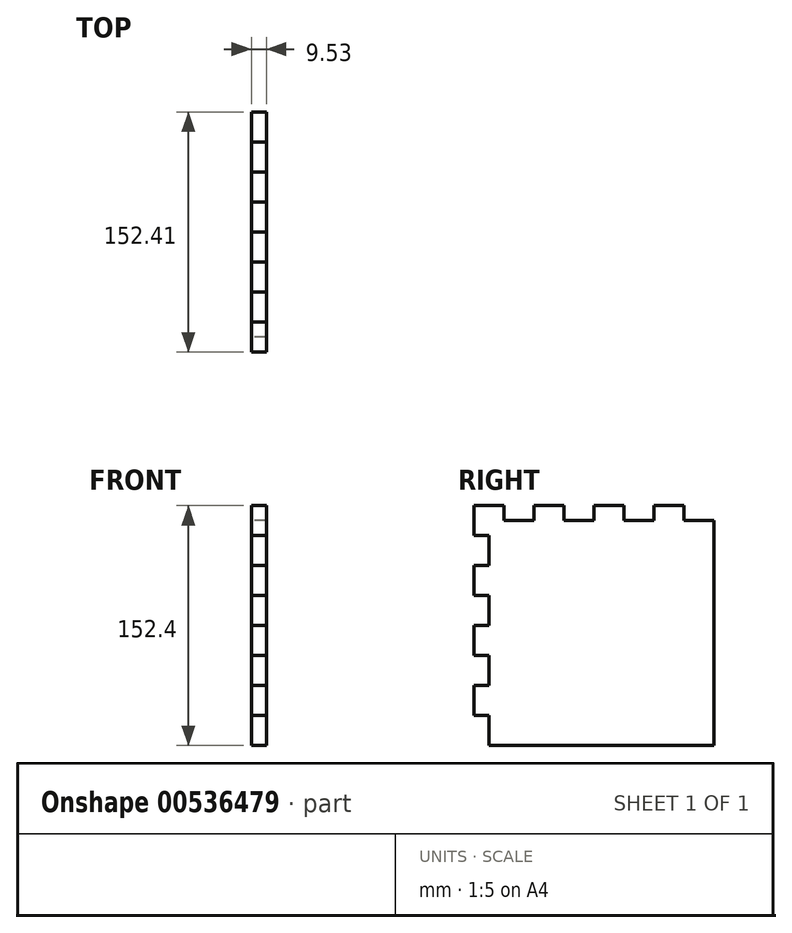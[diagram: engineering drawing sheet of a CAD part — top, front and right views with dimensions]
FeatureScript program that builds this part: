
annotation { "Feature Type Name" : "Feature", "Feature Type Description" : "" }
export const myFeature = defineFeature(function(context is Context, id is Id, definition is map)
    precondition{}
    {
        {
            var Q0;
            Q0=qCreatedBy(makeId("Right.planeOp"),FACE);
            var sketch = newSketch(context, id + "F0", { "sketchPlane" : qUnion([Q0])});
            skLineSegment(sketch, "E0", {"start": v(0, 0) * mm, "end": v(0, 19.05) * mm});
            skLineSegment(sketch, "E1", {"start": v(0, 19.05) * mm, "end": v(-9.53, 19.05) * mm});
            skLineSegment(sketch, "E2", {"start": v(-9.53, 19.05) * mm, "end": v(-9.53, 38.1) * mm});
            skLineSegment(sketch, "E3", {"start": v(-9.52, 38.1) * mm, "end": v(0, 38.1) * mm});
            skLineSegment(sketch, "E4", {"start": v(0, 38.1) * mm, "end": v(0, 57.15) * mm});
            skLineSegment(sketch, "E5", {"start": v(0, 57.15) * mm, "end": v(-9.52, 57.15) * mm});
            skLineSegment(sketch, "E6", {"start": v(-9.52, 57.15) * mm, "end": v(-9.52, 76.2) * mm});
            skLineSegment(sketch, "E7", {"start": v(-9.52, 76.2) * mm, "end": v(0, 76.2) * mm});
            skLineSegment(sketch, "E8", {"start": v(0, 76.2) * mm, "end": v(0, 95.25) * mm});
            skLineSegment(sketch, "E9", {"start": v(0, 95.25) * mm, "end": v(-9.53, 95.25) * mm});
            skLineSegment(sketch, "E10", {"start": v(-9.53, 95.25) * mm, "end": v(-9.53, 114.3) * mm});
            skLineSegment(sketch, "E11", {"start": v(-9.53, 152.4) * mm, "end": v(9.52, 152.4) * mm});
            skLineSegment(sketch, "E12", {"start": v(9.52, 152.4) * mm, "end": v(9.52, 142.88) * mm});
            skLineSegment(sketch, "E13", {"start": v(9.52, 142.88) * mm, "end": v(28.57, 142.88) * mm});
            skLineSegment(sketch, "E14", {"start": v(28.57, 142.88) * mm, "end": v(28.57, 152.4) * mm});
            skLineSegment(sketch, "E15", {"start": v(28.57, 152.4) * mm, "end": v(47.62, 152.4) * mm});
            skLineSegment(sketch, "E16", {"start": v(142.88, 142.88) * mm, "end": v(142.88, 0) * mm});
            skLineSegment(sketch, "E17", {"start": v(-9.53, 114.3) * mm, "end": v(0, 114.3) * mm});
            skLineSegment(sketch, "E18", {"start": v(0, 114.3) * mm, "end": v(0, 133.35) * mm});
            skLineSegment(sketch, "E19", {"start": v(0, 133.35) * mm, "end": v(-9.53, 133.35) * mm});
            skLineSegment(sketch, "E20.trimOffspring", {"start": v(-9.53, 133.35) * mm, "end": v(-9.53, 152.4) * mm});
            skLineSegment(sketch, "E21", {"start": v(47.62, 152.4) * mm, "end": v(47.62, 142.88) * mm});
            skLineSegment(sketch, "E22", {"start": v(47.62, 142.88) * mm, "end": v(66.67, 142.88) * mm});
            skLineSegment(sketch, "E23", {"start": v(66.67, 142.88) * mm, "end": v(66.67, 152.4) * mm});
            skLineSegment(sketch, "E24", {"start": v(85.72, 152.4) * mm, "end": v(85.72, 142.88) * mm});
            skLineSegment(sketch, "E25", {"start": v(85.72, 142.88) * mm, "end": v(104.78, 142.88) * mm});
            skLineSegment(sketch, "E26", {"start": v(104.78, 142.88) * mm, "end": v(104.78, 152.4) * mm});
            skLineSegment(sketch, "E27.trimOffspring", {"start": v(66.67, 152.4) * mm, "end": v(85.72, 152.4) * mm});
            skLineSegment(sketch, "E28.trimOffspring", {"start": v(104.78, 152.4) * mm, "end": v(123.83, 152.4) * mm});
            skLineSegment(sketch, "E29", {"start": v(123.83, 152.4) * mm, "end": v(123.83, 142.88) * mm});
            skLineSegment(sketch, "E30", {"start": v(123.83, 142.88) * mm, "end": v(142.88, 142.88) * mm});
            skPoint(sketch, "E31.orphan", {"position": v(142.88, 152.4) * mm});
            skLineSegment(sketch, "E32", {"start": v(0, 0) * mm, "end": v(142.88, 0) * mm, "construction": true});
            skLineSegment(sketch, "E33", {"start": v(0, 0) * mm, "end": v(0, 0) * mm});
            skLineSegment(sketch, "E34", {"start": v(0, 0) * mm, "end": v(142.88, 0) * mm});
            skLineSegment(sketch, "E35", {"start": v(142.88, 0) * mm, "end": v(142.88, 0) * mm});
            skSolve(sketch);
        }
        {
            var Q0;
            Q0 = qSketchRegion(id + "F0", true);
            extrude(context, id + "F1", {"entities" : qUnion([Q0]), "depth" : 9.52 * mm, "offsetDistance" : 25.4 * mm});
        }
    });
